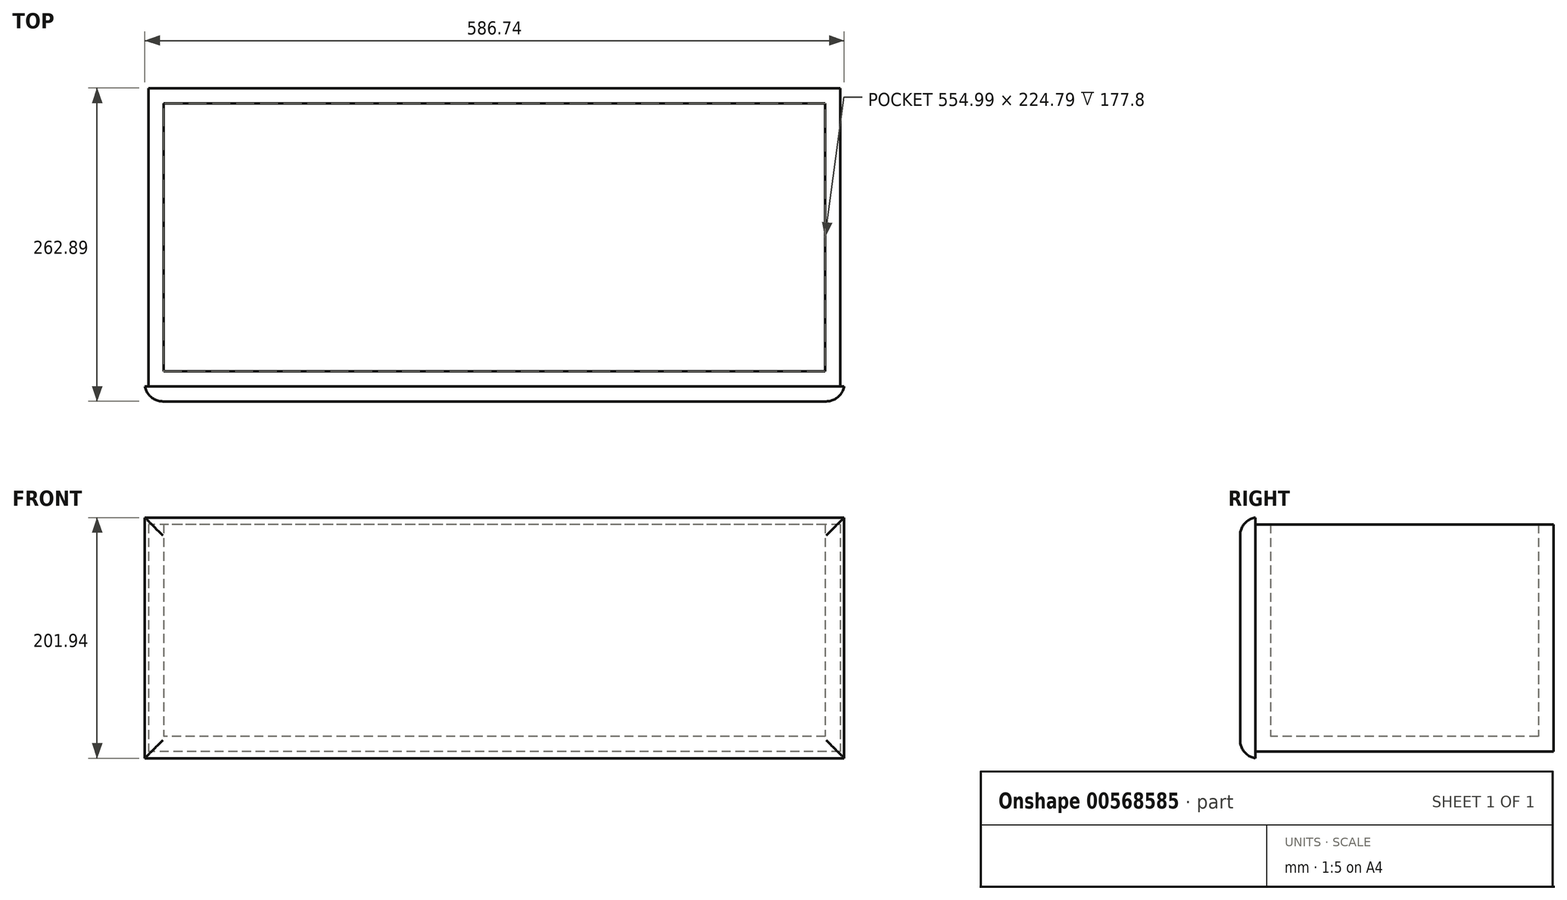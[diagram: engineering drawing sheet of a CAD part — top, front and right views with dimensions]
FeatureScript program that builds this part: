
annotation { "Feature Type Name" : "Feature", "Feature Type Description" : "" }
export const myFeature = defineFeature(function(context is Context, id is Id, definition is map)
    precondition{}
    {
        {
            var Q0;
            Q0=qCreatedBy(makeId("Top.planeOp"),FACE);
            var sketch = newSketch(context, id + "F0", { "sketchPlane" : qUnion([Q0])});
            skLineSegment(sketch, "E0.bottom", {"start": v(290.2, 125.1) * mm, "end": v(-290.2, 125.1) * mm});
            skLineSegment(sketch, "E0.top", {"start": v(290.2, -125.1) * mm, "end": v(-290.2, -125.1) * mm});
            skLineSegment(sketch, "E0.left", {"start": v(290.2, 125.1) * mm, "end": v(290.2, -125.1) * mm});
            skLineSegment(sketch, "E0.right", {"start": v(-290.2, 125.1) * mm, "end": v(-290.2, -125.1) * mm});
            skPoint(sketch, "E0.middle", {"position": v(0, 0) * mm});
            skSolve(sketch);
        }
        {
            var Q0;
            Q0=makeQuery(id+"F0.imprint","IMPRINT",FACE,{"disambiguationData":[TD([[makeQuery(id+"F0.imprint","IMPRINT",EDGE,{"derivedFrom":sQuery(id+"F0.wireOp",EDGE,"E0.bottom")}),1.0]])]});
            extrude(context, id + "F1", {"entities" : qUnion([Q0]), "depth" : 190.5 * mm, "offsetDistance" : 25.4 * mm, "symmetric" : true});
        }
        {
            var Q0;
            Q0=makeQuery(id+"F1.opExtrude","CAP_FACE",FACE,{"disambiguationData":[OSD([sQuery(id+"F0.wireOp",EDGE,"E0.bottom"),sQuery(id+"F0.wireOp",EDGE,"E0.top"),sQuery(id+"F0.wireOp",EDGE,"E0.left"),sQuery(id+"F0.wireOp",EDGE,"E0.right")])],"isStart":false});
            shell(context, id + "F2", {"entities" : qUnion([Q0]), "thickness" : 12.7 * mm});
        }
        {
            var Q0;
            Q0=makeQuery(id+"F1.opExtrude","SWEPT_FACE",FACE,{"disambiguationData":[OSD([sQuery(id+"F0.wireOp",EDGE,"E0.top")])]});
            var sketch = newSketch(context, id + "F3", { "sketchPlane" : qUnion([Q0])});
            skLineSegment(sketch, "E1", {"start": v(-271.15, 95.25) * mm, "end": v(-271.15, -76.2) * mm});
            skLineSegment(sketch, "E2", {"start": v(-271.15, -76.2) * mm, "end": v(271.15, -76.2) * mm});
            skLineSegment(sketch, "E3", {"start": v(271.15, -76.2) * mm, "end": v(271.15, 95.25) * mm});
            skSolve(sketch);
        }
        {
            var Q0;
            {var subQ0=sQuery(id+"F3.wireOp",EDGE,"E1");Q0=makeQuery(id+"F3.imprint","IMPRINT",FACE,{"disambiguationData":[TD([[makeQuery(id+"F3.imprint","IMPRINT",EDGE,{"derivedFrom":subQ0}),1.0]])]});}
            extrude(context, id + "F4", {"entities" : qUnion([Q0]), "operationType" : NewBodyOperationType.REMOVE, "oppositeDirection" : true, "depth" : 25.4 * mm, "offsetDistance" : 25.4 * mm});
        }
        {
            var Q0;
            Q0=makeQuery(id+"F1.opExtrude","SWEPT_FACE",FACE,{"disambiguationData":[OSD([sQuery(id+"F0.wireOp",EDGE,"E0.top")])]});
            var sketch = newSketch(context, id + "F5", { "sketchPlane" : qUnion([Q0])});
            skLineSegment(sketch, "E4.bottom", {"start": v(293.37, 100.97) * mm, "end": v(-293.37, 100.97) * mm});
            skLineSegment(sketch, "E4.top", {"start": v(293.37, -100.97) * mm, "end": v(-293.37, -100.97) * mm});
            skLineSegment(sketch, "E4.left", {"start": v(293.37, 100.97) * mm, "end": v(293.37, -100.97) * mm});
            skLineSegment(sketch, "E4.right", {"start": v(-293.37, 100.97) * mm, "end": v(-293.37, -100.97) * mm});
            skPoint(sketch, "E4.middle", {"position": v(0, 0) * mm});
            skSolve(sketch);
        }
        {
            var Q0;
            Q0=makeQuery(id+"F5.imprint","IMPRINT",FACE,{"disambiguationData":[TD([[makeQuery(id+"F5.imprint","IMPRINT",EDGE,{"derivedFrom":sQuery(id+"F5.wireOp",EDGE,"E4.bottom")}),1.0]])]});
            var Q1;
            {var subQ1=sQuery(id+"F0.wireOp",EDGE,"E0.top");Q1=makeQuery(id+"F5.imprint","IMPRINT",FACE,{"disambiguationData":[TD([[makeQuery(id+"F5.imprint","IMPRINT",EDGE,{"derivedFrom":makeQuery(id+"F1.opExtrude","CAP_EDGE",EDGE,{"disambiguationData":[OSD([subQ1])],"isStart":true})}),-1.0]])]});}
            extrude(context, id + "F6", {"entities" : qUnion([Q0, Q1]), "operationType" : NewBodyOperationType.ADD, "depth" : 12.7 * mm, "offsetDistance" : 25.4 * mm});
        }
        {
            var Q0;
            Q0=makeQuery(id+"F6.opExtrude","CAP_EDGE",EDGE,{"disambiguationData":[OSD([sQuery(id+"F5.wireOp",EDGE,"E4.bottom")])],"isStart":false});
            var Q1;
            Q1=makeQuery(id+"F6.opExtrude","CAP_EDGE",EDGE,{"disambiguationData":[OSD([sQuery(id+"F5.wireOp",EDGE,"E4.right")])],"isStart":false});
            var Q2;
            Q2=makeQuery(id+"F6.opExtrude","CAP_EDGE",EDGE,{"disambiguationData":[OSD([sQuery(id+"F5.wireOp",EDGE,"E4.top")])],"isStart":false});
            var Q3;
            Q3=makeQuery(id+"F6.opExtrude","CAP_EDGE",EDGE,{"disambiguationData":[OSD([sQuery(id+"F5.wireOp",EDGE,"E4.left")])],"isStart":false});
            fillet(context, id + "F7", {"entities" : qUnion([Q0, Q1, Q2, Q3]), "radius" : 15.24 * mm, "tangentPropagation" : true, "allowEdgeOverflow" : false});
        }
        {
            var Q0;
            Q0=makeQuery(id+"F4.boolean.opBoolean","COPY",FACE,{"derivedFrom":makeQuery(id+"F4.opExtrude","SWEPT_FACE",FACE,{"disambiguationData":[OSD([sQuery(id+"F3.wireOp",EDGE,"E2")])]})});
            extrude(context, id + "F8", {"entities" : qUnion([Q0]), "operationType" : NewBodyOperationType.ADD, "depth" : 171.45 * mm, "offsetDistance" : 25.4 * mm});
        }
    });
